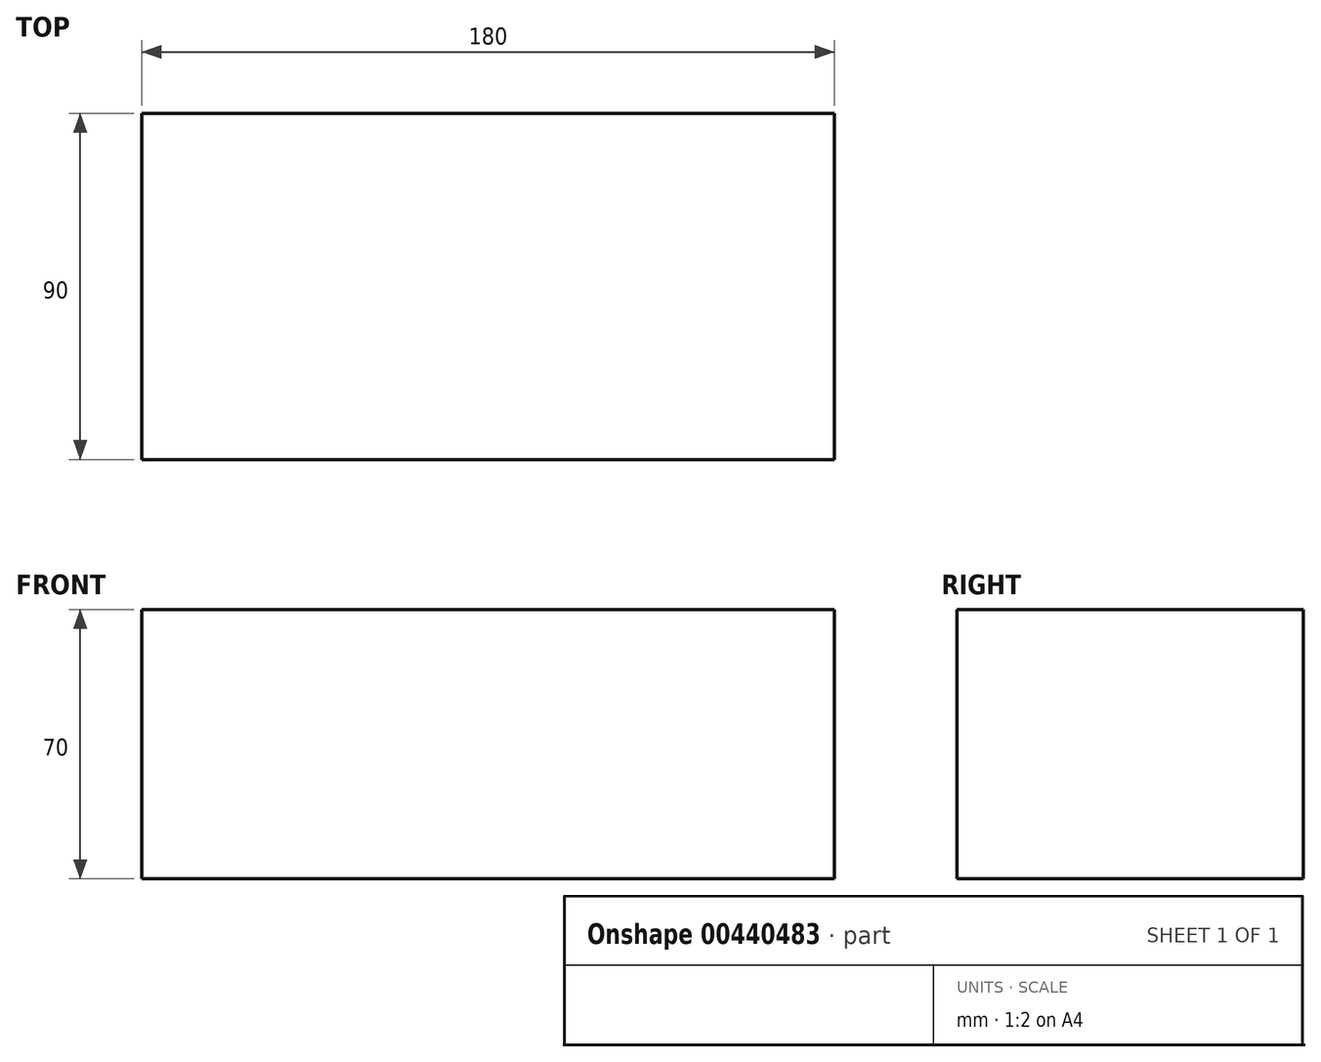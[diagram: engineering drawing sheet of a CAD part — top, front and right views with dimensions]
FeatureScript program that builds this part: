
annotation { "Feature Type Name" : "Feature", "Feature Type Description" : "" }
export const myFeature = defineFeature(function(context is Context, id is Id, definition is map)
    precondition{}
    {
        {
            var Q0;
            Q0=qCreatedBy(makeId("Top.planeOp"),FACE);
            var sketch = newSketch(context, id + "F0", { "sketchPlane" : qUnion([Q0])});
            skLineSegment(sketch, "E0.bottom", {"start": v(-90, -45) * mm, "end": v(90, -45) * mm});
            skLineSegment(sketch, "E0.top", {"start": v(-90, 45) * mm, "end": v(90, 45) * mm});
            skLineSegment(sketch, "E0.left", {"start": v(-90, -45) * mm, "end": v(-90, 45) * mm});
            skLineSegment(sketch, "E0.right", {"start": v(90, -45) * mm, "end": v(90, 45) * mm});
            skPoint(sketch, "E0.middle", {"position": v(0, 0) * mm});
            skSolve(sketch);
        }
        {
            var Q0;
            Q0 = qSketchRegion(id + "F0", true);
            extrude(context, id + "F1", {"entities" : qUnion([Q0]), "depth" : 70 * mm, "offsetDistance" : 25 * mm});
        }
    });
